# Revit family: НЕВАТОМ_Вентилятор VR-KP, Версия 2
name_source: partatom
category: Оборудование
revit_build: Autodesk Revit 2017 (Build: 20170118_1100(x64)
units: mm (PartAtom-declared; Revit-internal decimal feet)

## family parameters
Всегда вертикально = Да
На основе рабочей плоскости = Нет
Общий = Да
При загрузке вырезать с полостями = Нет
Размер круглого соединителя = Использовать диаметр
Тип детали = Нормальный
Точка расчета площади = Нет

## types (14) — shared parameters
ADSK_Единица измерения = шт.
ADSK_Завод-изготовитель = НЕВАТОМ
ADSK_Количество = 1
ADSK_Материал наименование = Оцинкованная сталь
ADSK_Наименование = Вентилятор кухонный
ADSK_Потеря давления воздуха = 0.0 Па
ADSK_Расход воздуха = 0.0 л/с
L уголка = 60 мм
Nevatom_URL = https://t.me

## per-type parameters (varying)
| type | ADSK_Количество фаз | ADSK_Марка | ADSK_Масса | ADSK_Напряжение | ADSK_Полная мощность | ADSK_Размер_Высота | ADSK_Размер_Длина | ADSK_Размер_Ширина | ADSK_Ток | ADSK_Частота вращения вентилятора | B | B1 | Dвнеш | Dвнутр | L | L1 | L2 |
| VR-KP 250 -0,55/3000 | 3 | VR-KP 250 -0,55/3000 | 35.5 | 380 В | 0.550 кВт | 450 мм | 510 мм | 450 мм | 1 А | 3000 | 450 мм | 390 мм | 250 мм | 390 мм | 510 мм | 142 мм | 450 мм |
| VR-KP 280 -0,75/3000 | 3 | VR-KP 280 -0,75/3000 | 39.8 | 380 В | 0.750 кВт | 450 мм | 510 мм | 450 мм | 2 А | 3000 | 450 мм | 390 мм | 280 мм | 390 мм | 510 мм | 169 мм | 450 мм |
| VR-KP 315 -0,75/3000 | 3 | VR-KP 315-0,75/3000 | 50.5 | 380 В | 0.750 кВт | 550 мм | 600 мм | 550 мм | 2 А | 3000 | 550 мм | 490 мм | 315 мм | 490 мм | 600 мм | 186 мм | 540 мм |
| VR-KP 315 -1,5/3000 | 1 | VR-KP 315 -1,5/3000 | 55.4 | 380 В | 1.500 кВт | 550 мм | 600 мм | 550 мм | 3 А | 3000 | 550 мм | 490 мм | 315 мм | 490 мм | 600 мм | 196 мм | 540 мм |
| VR-KP 355 -2,2/3000 | 3 | VR-KP 355 -2,2/3000 | 59.8 | 380 В | 2.200 кВт | 550 мм | 600 мм | 550 мм | 5 А | 3000 | 550 мм | 490 мм | 355 мм | 490 мм | 600 мм | 221 мм | 540 мм |
| VR-KP 400 -0,55/1500 | 3 | VR-KP 400 -0,55/1500 | 67 | 380 В | 0.550 кВт | 700 мм | 650 мм | 700 мм | 2 А | 1500 | 700 мм | 640 мм | 400 мм | 640 мм | 650 мм | 235 мм | 590 мм |
| VR-KP 450 -0,75/1500 | 3 | VR-KP 450 -0,75/1500 | 76.1 | 380 В | 0.750 кВт | 700 мм | 650 мм | 700 мм | 2 А | 1500 | 700 мм | 640 мм | 450 мм | 640 мм | 650 мм | 258 мм | 590 мм |
| VR-KP 500 -0,37/1000 | 3 | VR-KP 500 -0,37/1000 | 97.4 | 380 В | 0.370 кВт | 850 мм | 800 мм | 850 мм | 1 А | 1000 | 850 мм | 790 мм | 500 мм | 790 мм | 800 мм | 287 мм | 740 мм |
| VR-KP 500 -1,5/1500 | 3 | VR-KP 500 -1,5/1500 | 105.1 | 380 В | 1.500 кВт | 850 мм | 800 мм | 850 мм | 4 А | 1500 | 850 мм | 790 мм | 500 мм | 790 мм | 800 мм | 307 мм | 740 мм |
| VR-KP 560 -1,1/1000 | 3 | VR-KP 560-1,1/1000 | 109.7 | 1140 В | 1.100 кВт | 850 мм | 800 мм | 850 мм | 3 А | 1000 | 850 мм | 790 мм | 560 мм | 790 мм | 800 мм | 334 мм | 740 мм |
| VR-KP 560 -3/1500 | 3 | VR-KP 560 -3/1500 | 123.9 | 380 В | 3.000 кВт | 850 мм | 800 мм | 850 мм | 7 А | 1500 | 850 мм | 790 мм | 560 мм | 790 мм | 800 мм | 344 мм | 740 мм |
| VR-KP 630 -1,5/1000 | 3 | VR-KP 630 -1,5/1000 | 151.6 | 380 В | 1.500 кВт | 1050 мм | 950 мм | 1050 мм | 14 А | 1000 | 1050 мм | 990 мм | 630 мм | 990 мм | 950 мм | 370 мм | 890 мм |
| VR-KP 630 -5,5/1500 | 3 | VR-KP 630 -5,5/1500 | 178.7 | 380 В | 5.500 кВт | 1050 мм | 950 мм | 1050 мм | 12 А | 1500 | 1050 мм | 990 мм | 630 мм | 990 мм | 950 мм | 400 мм | 890 мм |
| VR-KP 710 -3/1000 | 3 | VR-KP 710 -3/1000 | 195.6 | 380 В | 3.000 кВт | 1050 мм | 950 мм | 1050 мм | 7 А | 1000 | 1050 мм | 990 мм | 710 мм | 990 мм | 950 мм | 439 мм | 890 мм |
